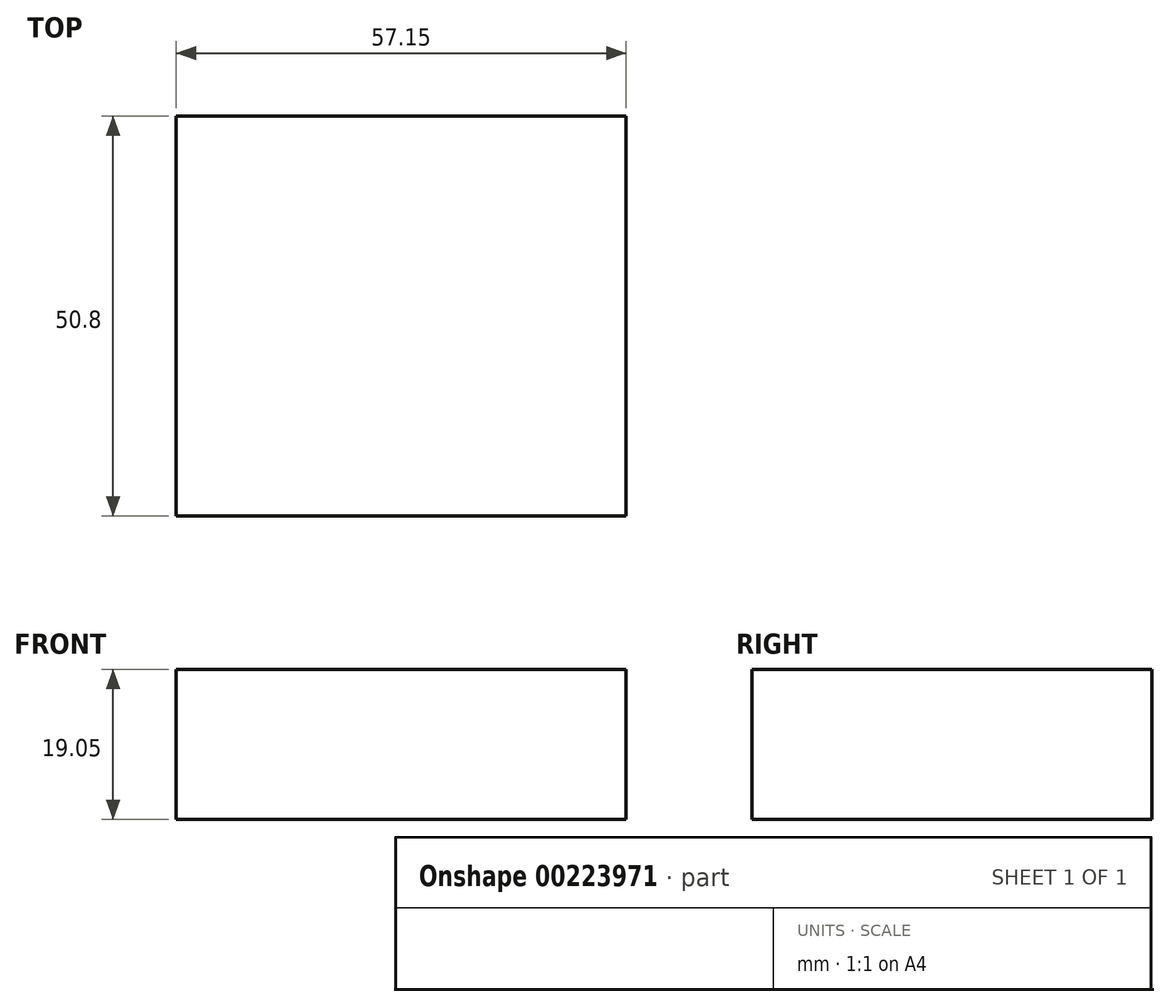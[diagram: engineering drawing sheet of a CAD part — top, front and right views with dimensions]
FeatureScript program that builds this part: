
annotation { "Feature Type Name" : "Feature", "Feature Type Description" : "" }
export const myFeature = defineFeature(function(context is Context, id is Id, definition is map)
    precondition{}
    {
        {
            var Q0;
            Q0=qCreatedBy(makeId("Front.planeOp"),FACE);
            var sketch = newSketch(context, id + "F0", { "sketchPlane" : qUnion([Q0])});
            skLineSegment(sketch, "E0.bottom", {"start": v(-18.44, 19.28) * mm, "end": v(-75.59, 19.28) * mm});
            skLineSegment(sketch, "E0.top", {"start": v(-18.44, 38.33) * mm, "end": v(-75.59, 38.33) * mm});
            skLineSegment(sketch, "E0.left", {"start": v(-18.44, 19.28) * mm, "end": v(-18.44, 38.33) * mm});
            skLineSegment(sketch, "E0.right", {"start": v(-75.59, 19.28) * mm, "end": v(-75.59, 38.33) * mm});
            skPoint(sketch, "E0.middle", {"position": v(-47.01, 28.8) * mm});
            skSolve(sketch);
        }
        {
            var Q0;
            Q0 = qSketchRegion(id + "F0", true);
            extrude(context, id + "F1", {"entities" : qUnion([Q0]), "endBound" : BoundingType.SYMMETRIC, "depth" : 50.8 * mm});
        }
    });
